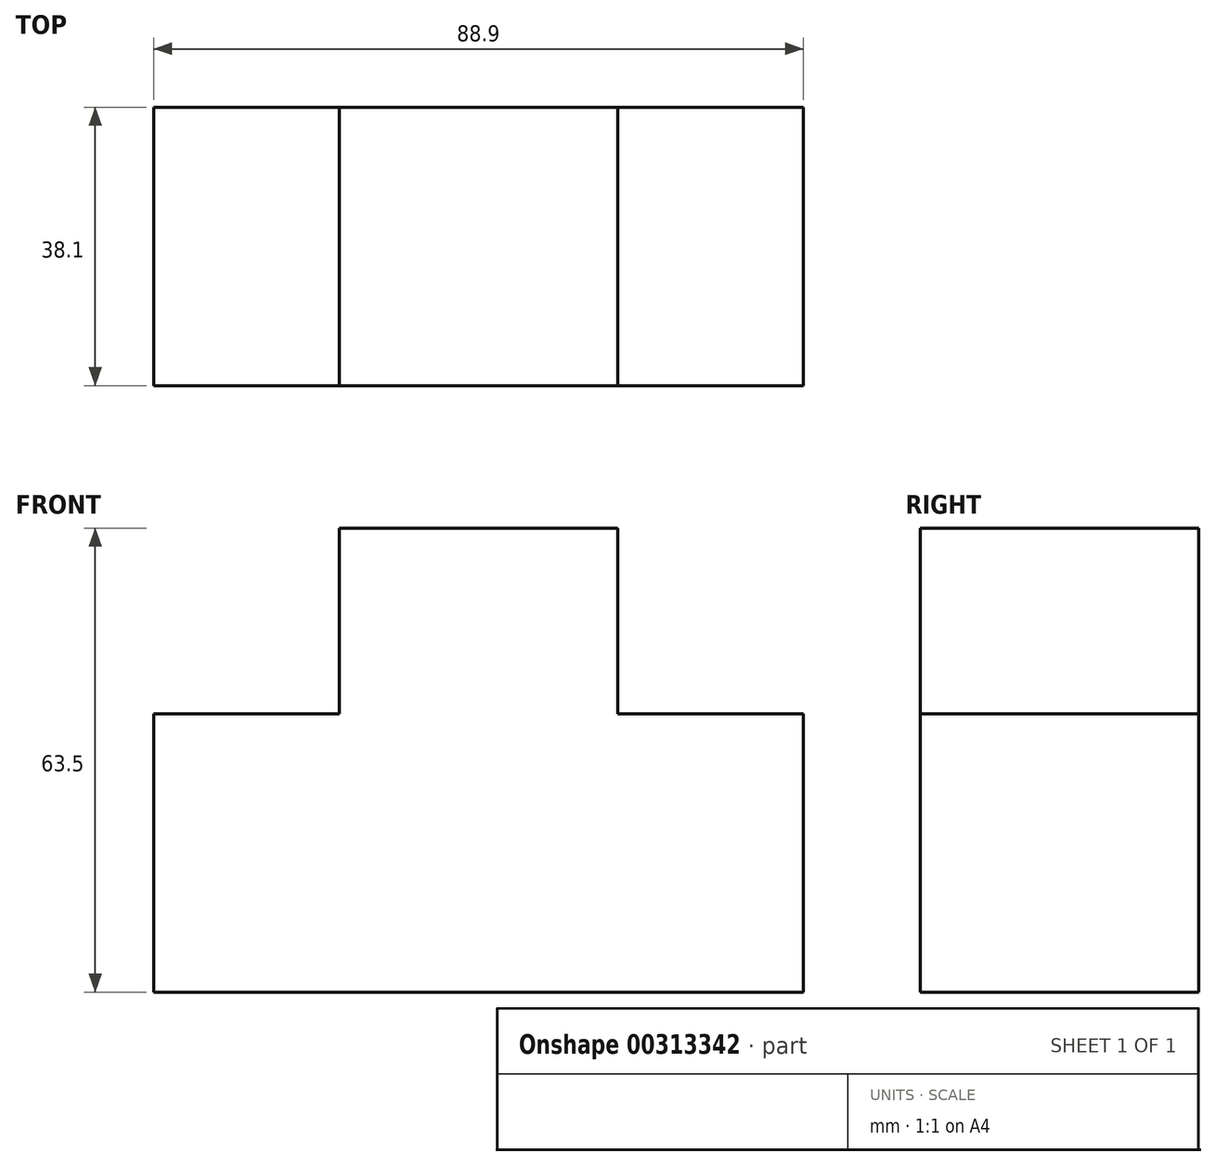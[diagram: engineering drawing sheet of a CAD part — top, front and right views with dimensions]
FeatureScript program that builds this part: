
annotation { "Feature Type Name" : "Feature", "Feature Type Description" : "" }
export const myFeature = defineFeature(function(context is Context, id is Id, definition is map)
    precondition{}
    {
        {
            var Q0;
            Q0=qCreatedBy(makeId("Front.planeOp"),FACE);
            var sketch = newSketch(context, id + "F0", { "sketchPlane" : qUnion([Q0])});
            skLineSegment(sketch, "E0", {"start": v(-40.65, -44.4) * mm, "end": v(48.25, -44.4) * mm});
            skLineSegment(sketch, "E1", {"start": v(-40.65, -44.4) * mm, "end": v(-40.65, -6.3) * mm});
            skLineSegment(sketch, "E2", {"start": v(-40.65, -6.3) * mm, "end": v(-15.25, -6.3) * mm});
            skLineSegment(sketch, "E3", {"start": v(-15.25, -6.3) * mm, "end": v(-15.25, 19.1) * mm});
            skLineSegment(sketch, "E4", {"start": v(-15.25, 19.1) * mm, "end": v(22.85, 19.1) * mm});
            skLineSegment(sketch, "E5", {"start": v(22.85, 19.1) * mm, "end": v(22.85, -6.3) * mm});
            skLineSegment(sketch, "E6", {"start": v(22.85, -6.3) * mm, "end": v(48.25, -6.3) * mm});
            skLineSegment(sketch, "E7", {"start": v(48.25, -6.3) * mm, "end": v(48.25, -44.4) * mm});
            skSolve(sketch);
        }
        {
            var Q0;
            Q0=makeQuery(id+"F0.imprint","IMPRINT",FACE,{"disambiguationData":[TD([[makeQuery(id+"F0.imprint","IMPRINT",EDGE,{"derivedFrom":sQuery(id+"F0.wireOp",EDGE,"E0")}),1.0]])]});
            extrude(context, id + "F1", {"entities" : qUnion([Q0]), "depth" : 38.1 * mm});
        }
    });
